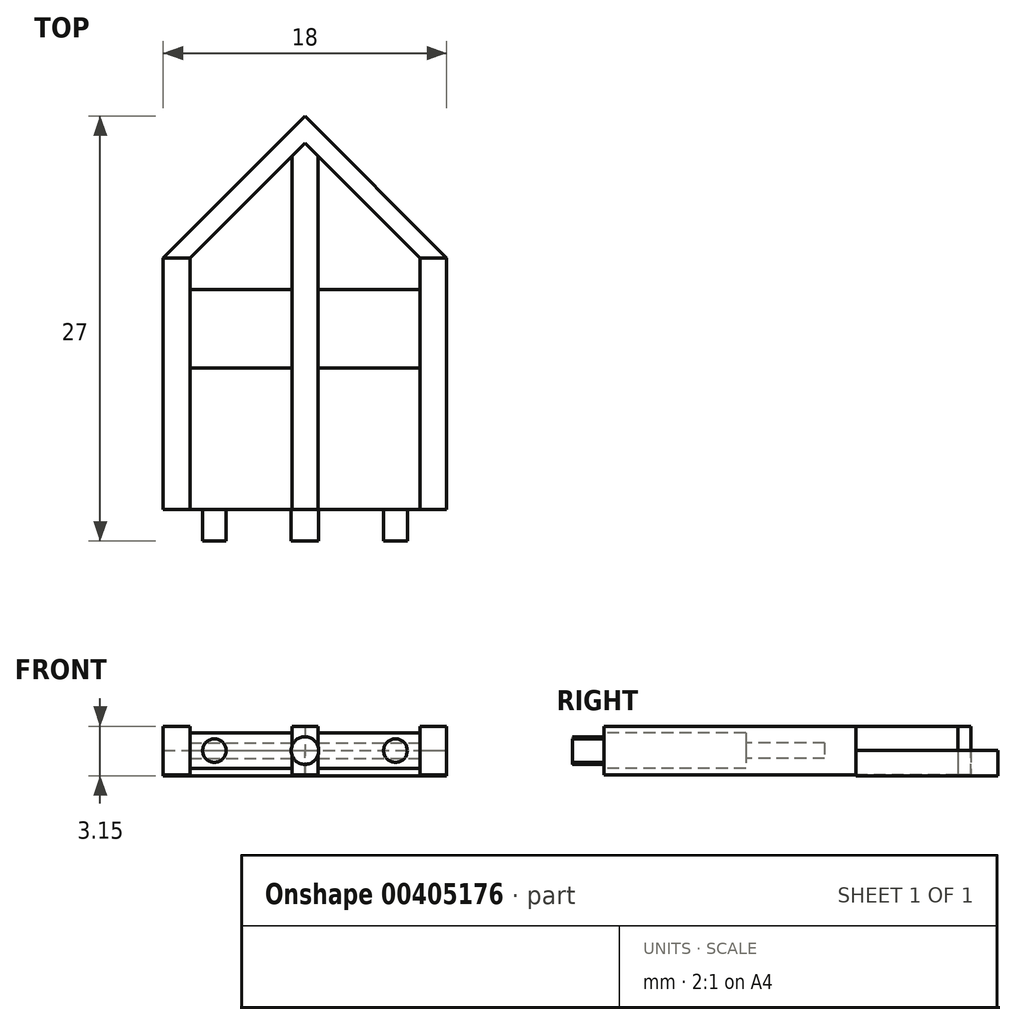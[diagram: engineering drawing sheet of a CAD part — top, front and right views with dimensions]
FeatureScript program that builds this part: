
annotation { "Feature Type Name" : "Feature", "Feature Type Description" : "" }
export const myFeature = defineFeature(function(context is Context, id is Id, definition is map)
    precondition{}
    {
        {
            var Q0;
            Q0=qCreatedBy(makeId("Top.planeOp"),FACE);
            var sketch = newSketch(context, id + "F0", { "sketchPlane" : qUnion([Q0])});
            skLineSegment(sketch, "E0", {"start": v(0, 0) * mm, "end": v(18, 0) * mm});
            skLineSegment(sketch, "E1", {"start": v(18, 0) * mm, "end": v(18, 16) * mm});
            skLineSegment(sketch, "E2", {"start": v(0, 16) * mm, "end": v(0, 0) * mm});
            skLineSegment(sketch, "E3", {"start": v(0, 16) * mm, "end": v(9, 25) * mm});
            skLineSegment(sketch, "E4", {"start": v(9, 25) * mm, "end": v(18, 16) * mm});
            skLineSegment(sketch, "E5", {"start": v(0, 9) * mm, "end": v(18, 9) * mm});
            skLineSegment(sketch, "E6", {"start": v(9, 25) * mm, "end": v(9, 0) * mm});
            skLineSegment(sketch, "E7", {"start": v(8.13, 0) * mm, "end": v(8.13, -2) * mm});
            skLineSegment(sketch, "E8", {"start": v(8.13, -2) * mm, "end": v(9.88, -2) * mm});
            skLineSegment(sketch, "E9", {"start": v(9.88, -2) * mm, "end": v(9.88, 0) * mm});
            skLineSegment(sketch, "E10", {"start": v(2.5, 0) * mm, "end": v(2.5, -2) * mm});
            skLineSegment(sketch, "E11", {"start": v(2.5, -2) * mm, "end": v(4, -2) * mm});
            skLineSegment(sketch, "E12", {"start": v(4, -2) * mm, "end": v(4, 0) * mm});
            skLineSegment(sketch, "E13", {"start": v(14, 0) * mm, "end": v(14, -2) * mm});
            skLineSegment(sketch, "E14", {"start": v(14, -2) * mm, "end": v(15.5, -2) * mm});
            skLineSegment(sketch, "E15", {"start": v(15.5, -2) * mm, "end": v(15.5, 0) * mm});
            skLineSegment(sketch, "E16", {"start": v(8.18, 22.47) * mm, "end": v(8.18, 0) * mm});
            skLineSegment(sketch, "E17", {"start": v(9.82, 22.47) * mm, "end": v(9.83, 0) * mm});
            skLineSegment(sketch, "E18", {"start": v(1.7, 16) * mm, "end": v(9, 23.3) * mm});
            skLineSegment(sketch, "E19", {"start": v(9, 23.3) * mm, "end": v(16.3, 16) * mm});
            skLineSegment(sketch, "E20", {"start": v(1.7, 16) * mm, "end": v(1.7, 0) * mm});
            skLineSegment(sketch, "E21", {"start": v(16.3, 16) * mm, "end": v(16.3, 0) * mm});
            skLineSegment(sketch, "E22", {"start": v(0, 14) * mm, "end": v(18, 14) * mm});
            skLineSegment(sketch, "E23", {"start": v(0, 16) * mm, "end": v(1.7, 16) * mm});
            skLineSegment(sketch, "E24", {"start": v(16.3, 16) * mm, "end": v(18, 16) * mm});
            skSolve(sketch);
        }
        {
            var Q0;
            {var subQ0=sQuery(id+"F0.wireOp",EDGE,"E2");var subQ1=sQuery(id+"F0.wireOp",EDGE,"E0");var subQ2=makeQuery(id+"F0.imprint","INTERSECT",VERTEX,{"derivedFrom":[subQ1,subQ0]});Q0=makeQuery(id+"F0.imprint","IMPRINT",FACE,{"disambiguationData":[TD([[makeQuery(id+"F0.imprint","IMPRINT",EDGE,{"disambiguationData":[TD([[subQ2,-1.0]])],"derivedFrom":subQ1}),1.0]])]});}
            var Q1;
            {var subQ0=sQuery(id+"F0.wireOp",EDGE,"E23");Q1=makeQuery(id+"F0.imprint","IMPRINT",FACE,{"disambiguationData":[TD([[makeQuery(id+"F0.imprint","IMPRINT",EDGE,{"derivedFrom":subQ0}),-1.0]])]});}
            var Q2;
            {var subQ0=sQuery(id+"F0.wireOp",EDGE,"E5");var subQ1=sQuery(id+"F0.wireOp",EDGE,"E2");var subQ2=makeQuery(id+"F0.imprint","INTERSECT",VERTEX,{"derivedFrom":[subQ1,subQ0]});Q2=makeQuery(id+"F0.imprint","IMPRINT",FACE,{"disambiguationData":[TD([[makeQuery(id+"F0.imprint","IMPRINT",EDGE,{"disambiguationData":[TD([[subQ2,1.0]])],"derivedFrom":subQ1}),1.0]])]});}
            var Q3;
            {var subQ0=sQuery(id+"F0.wireOp",EDGE,"E1");var subQ1=sQuery(id+"F0.wireOp",EDGE,"E0");var subQ2=makeQuery(id+"F0.imprint","INTERSECT",VERTEX,{"derivedFrom":[subQ1,subQ0]});Q3=makeQuery(id+"F0.imprint","IMPRINT",FACE,{"disambiguationData":[TD([[makeQuery(id+"F0.imprint","IMPRINT",EDGE,{"disambiguationData":[TD([[subQ2,1.0]])],"derivedFrom":subQ1}),1.0]])]});}
            var Q4;
            {var subQ0=sQuery(id+"F0.wireOp",EDGE,"E24");Q4=makeQuery(id+"F0.imprint","IMPRINT",FACE,{"disambiguationData":[TD([[makeQuery(id+"F0.imprint","IMPRINT",EDGE,{"derivedFrom":subQ0}),-1.0]])]});}
            var Q5;
            {var subQ0=sQuery(id+"F0.wireOp",EDGE,"E5");var subQ1=sQuery(id+"F0.wireOp",EDGE,"E1");var subQ2=makeQuery(id+"F0.imprint","INTERSECT",VERTEX,{"derivedFrom":[subQ1,subQ0]});Q5=makeQuery(id+"F0.imprint","IMPRINT",FACE,{"disambiguationData":[TD([[makeQuery(id+"F0.imprint","IMPRINT",EDGE,{"disambiguationData":[TD([[subQ2,-1.0]])],"derivedFrom":subQ1}),1.0]])]});}
            var Q6;
            {var subQ0=sQuery(id+"F0.wireOp",EDGE,"E6");var subQ1=sQuery(id+"F0.wireOp",EDGE,"E0");var subQ2=makeQuery(id+"F0.imprint","INTERSECT",VERTEX,{"derivedFrom":[subQ1,subQ0]});Q6=makeQuery(id+"F0.imprint","IMPRINT",FACE,{"disambiguationData":[TD([[makeQuery(id+"F0.imprint","IMPRINT",EDGE,{"disambiguationData":[TD([[subQ2,1.0]])],"derivedFrom":subQ1}),1.0]])]});}
            var Q7;
            {var subQ0=sQuery(id+"F0.wireOp",EDGE,"E6");var subQ1=sQuery(id+"F0.wireOp",EDGE,"E0");var subQ2=makeQuery(id+"F0.imprint","INTERSECT",VERTEX,{"derivedFrom":[subQ1,subQ0]});Q7=makeQuery(id+"F0.imprint","IMPRINT",FACE,{"disambiguationData":[TD([[makeQuery(id+"F0.imprint","IMPRINT",EDGE,{"disambiguationData":[TD([[subQ2,-1.0]])],"derivedFrom":subQ1}),1.0]])]});}
            var Q8;
            {var subQ0=sQuery(id+"F0.wireOp",EDGE,"E6");var subQ1=sQuery(id+"F0.wireOp",EDGE,"E5");var subQ2=makeQuery(id+"F0.imprint","INTERSECT",VERTEX,{"derivedFrom":[subQ1,subQ0]});Q8=makeQuery(id+"F0.imprint","IMPRINT",FACE,{"disambiguationData":[TD([[makeQuery(id+"F0.imprint","IMPRINT",EDGE,{"disambiguationData":[TD([[subQ2,-1.0]])],"derivedFrom":subQ1}),1.0]])]});}
            var Q9;
            {var subQ0=sQuery(id+"F0.wireOp",EDGE,"E16");var subQ1=sQuery(id+"F0.wireOp",EDGE,"E5");var subQ2=makeQuery(id+"F0.imprint","INTERSECT",VERTEX,{"derivedFrom":[subQ1,subQ0]});Q9=makeQuery(id+"F0.imprint","IMPRINT",FACE,{"disambiguationData":[TD([[makeQuery(id+"F0.imprint","IMPRINT",EDGE,{"disambiguationData":[TD([[subQ2,-1.0]])],"derivedFrom":subQ1}),1.0]])]});}
            var Q10;
            {var subQ0=sQuery(id+"F0.wireOp",EDGE,"E18");var subQ5=sQuery(id+"F0.wireOp",EDGE,"E16");var subQ7=makeQuery(id+"F0.imprint","INTERSECT",VERTEX,{"derivedFrom":[subQ5,subQ0]});Q10=makeQuery(id+"F0.imprint","IMPRINT",FACE,{"disambiguationData":[TD([[makeQuery(id+"F0.imprint","IMPRINT",EDGE,{"disambiguationData":[TD([[subQ7,-1.0]])],"derivedFrom":subQ5}),1.0]])]});}
            var Q11;
            {var subQ0=sQuery(id+"F0.wireOp",EDGE,"E19");var subQ5=sQuery(id+"F0.wireOp",EDGE,"E17");var subQ6=makeQuery(id+"F0.imprint","INTERSECT",VERTEX,{"derivedFrom":[subQ5,subQ0]});Q11=makeQuery(id+"F0.imprint","IMPRINT",FACE,{"disambiguationData":[TD([[makeQuery(id+"F0.imprint","IMPRINT",EDGE,{"disambiguationData":[TD([[subQ6,-1.0]])],"derivedFrom":subQ5}),-1.0]])]});}
            extrude(context, id + "F1", {"entities" : qUnion([Q0, Q1, Q2, Q3, Q4, Q5, Q6, Q7, Q8, Q9, Q10, Q11]), "endBound" : BoundingType.SYMMETRIC, "depth" : 3.1 * mm});
        }
        {
            var Q0;
            {var subQ0=sQuery(id+"F0.wireOp",EDGE,"E0");var subQ5=makeQuery(id+"F0.imprint","INTERSECT",VERTEX,{"derivedFrom":[subQ0,sQuery(id+"F0.wireOp",EDGE,"E10")]});Q0=makeQuery(id+"F0.imprint","IMPRINT",FACE,{"disambiguationData":[TD([[makeQuery(id+"F0.imprint","IMPRINT",EDGE,{"disambiguationData":[TD([[subQ5,1.0]])],"derivedFrom":subQ0}),1.0]])]});}
            var Q1;
            {var subQ0=sQuery(id+"F0.wireOp",EDGE,"E0");var subQ7=makeQuery(id+"F0.imprint","INTERSECT",VERTEX,{"derivedFrom":[subQ0,sQuery(id+"F0.wireOp",EDGE,"E9")]});Q1=makeQuery(id+"F0.imprint","IMPRINT",FACE,{"disambiguationData":[TD([[makeQuery(id+"F0.imprint","IMPRINT",EDGE,{"disambiguationData":[TD([[subQ7,1.0]])],"derivedFrom":subQ0}),1.0]])]});}
            extrude(context, id + "F2", {"entities" : qUnion([Q0, Q1]), "endBound" : BoundingType.SYMMETRIC, "depth" : 2.25 * mm});
        }
        {
            var Q0;
            {var subQ5=sQuery(id+"F0.wireOp",EDGE,"E3");Q0=makeQuery(id+"F0.imprint","IMPRINT",FACE,{"disambiguationData":[TD([[makeQuery(id+"F0.imprint","IMPRINT",EDGE,{"derivedFrom":subQ5}),-1.0]])]});}
            var Q1;
            {var subQ4=sQuery(id+"F0.wireOp",EDGE,"E4");Q1=makeQuery(id+"F0.imprint","IMPRINT",FACE,{"disambiguationData":[TD([[makeQuery(id+"F0.imprint","IMPRINT",EDGE,{"derivedFrom":subQ4}),-1.0]])]});}
            extrude(context, id + "F3", {"entities" : qUnion([Q0, Q1]), "oppositeDirection" : true, "depth" : 1.6 * mm});
        }
        {
            var Q0;
            {var subQ0=sQuery(id+"F0.wireOp",EDGE,"E20");var subQ1=sQuery(id+"F0.wireOp",EDGE,"E5");var subQ2=makeQuery(id+"F0.imprint","INTERSECT",VERTEX,{"derivedFrom":[subQ1,subQ0]});Q0=makeQuery(id+"F0.imprint","IMPRINT",FACE,{"disambiguationData":[TD([[makeQuery(id+"F0.imprint","IMPRINT",EDGE,{"disambiguationData":[TD([[subQ2,-1.0]])],"derivedFrom":subQ1}),1.0]])]});}
            var Q1;
            {var subQ0=sQuery(id+"F0.wireOp",EDGE,"E17");var subQ1=sQuery(id+"F0.wireOp",EDGE,"E5");var subQ2=makeQuery(id+"F0.imprint","INTERSECT",VERTEX,{"derivedFrom":[subQ1,subQ0]});Q1=makeQuery(id+"F0.imprint","IMPRINT",FACE,{"disambiguationData":[TD([[makeQuery(id+"F0.imprint","IMPRINT",EDGE,{"disambiguationData":[TD([[subQ2,-1.0]])],"derivedFrom":subQ1}),1.0]])]});}
            extrude(context, id + "F4", {"entities" : qUnion([Q0, Q1]), "endBound" : BoundingType.SYMMETRIC, "depth" : 1 * mm});
        }
        {
            var Q0;
            {var subQ0=sQuery(id+"F0.wireOp",EDGE,"E10");Q0=makeQuery(id+"F0.imprint","IMPRINT",FACE,{"disambiguationData":[TD([[makeQuery(id+"F0.imprint","IMPRINT",EDGE,{"derivedFrom":subQ0}),1.0]])]});}
            var Q1;
            {var subQ0=sQuery(id+"F0.wireOp",EDGE,"E13");Q1=makeQuery(id+"F0.imprint","IMPRINT",FACE,{"disambiguationData":[TD([[makeQuery(id+"F0.imprint","IMPRINT",EDGE,{"derivedFrom":subQ0}),1.0]])]});}
            extrude(context, id + "F5", {"entities" : qUnion([Q0, Q1]), "endBound" : BoundingType.SYMMETRIC, "depth" : 1.5 * mm});
        }
        {
            var Q0;
            {var subQ5=sQuery(id+"F0.wireOp",EDGE,"E7");Q0=makeQuery(id+"F0.imprint","IMPRINT",FACE,{"disambiguationData":[TD([[makeQuery(id+"F0.imprint","IMPRINT",EDGE,{"derivedFrom":subQ5}),1.0]])]});}
            extrude(context, id + "F6", {"entities" : qUnion([Q0]), "endBound" : BoundingType.SYMMETRIC, "depth" : 1.75 * mm});
        }
        {
            var Q0;
            Q0=makeQuery(id+"F6.opExtrude","CAP_EDGE",EDGE,{"disambiguationData":[OSD([sQuery(id+"F0.wireOp",EDGE,"E9")])],"isStart":true});
            var Q1;
            Q1=makeQuery(id+"F6.opExtrude","CAP_EDGE",EDGE,{"disambiguationData":[OSD([sQuery(id+"F0.wireOp",EDGE,"E7")])],"isStart":true});
            var Q2;
            Q2=makeQuery(id+"F6.opExtrude","CAP_EDGE",EDGE,{"disambiguationData":[OSD([sQuery(id+"F0.wireOp",EDGE,"E9")])],"isStart":false});
            var Q3;
            Q3=makeQuery(id+"F6.opExtrude","CAP_EDGE",EDGE,{"disambiguationData":[OSD([sQuery(id+"F0.wireOp",EDGE,"E7")])],"isStart":false});
            fillet(context, id + "F7", {"entities" : qUnion([Q0, Q1, Q2, Q3]), "radius" : 0.88 * mm, "tangentPropagation" : true, "allowEdgeOverflow" : false});
        }
        {
            var Q0;
            Q0=makeQuery(id+"F5.opExtrude","CAP_EDGE",EDGE,{"disambiguationData":[OSD([sQuery(id+"F0.wireOp",EDGE,"E13")])],"isStart":false});
            var Q1;
            Q1=makeQuery(id+"F5.opExtrude","CAP_EDGE",EDGE,{"disambiguationData":[OSD([sQuery(id+"F0.wireOp",EDGE,"E15")])],"isStart":false});
            var Q2;
            Q2=makeQuery(id+"F5.opExtrude","CAP_EDGE",EDGE,{"disambiguationData":[OSD([sQuery(id+"F0.wireOp",EDGE,"E15")])],"isStart":true});
            var Q3;
            Q3=makeQuery(id+"F5.opExtrude","CAP_EDGE",EDGE,{"disambiguationData":[OSD([sQuery(id+"F0.wireOp",EDGE,"E13")])],"isStart":true});
            var Q4;
            Q4=makeQuery(id+"F5.opExtrude","CAP_EDGE",EDGE,{"disambiguationData":[OSD([sQuery(id+"F0.wireOp",EDGE,"E10")])],"isStart":false});
            var Q5;
            Q5=makeQuery(id+"F5.opExtrude","CAP_EDGE",EDGE,{"disambiguationData":[OSD([sQuery(id+"F0.wireOp",EDGE,"E12")])],"isStart":false});
            var Q6;
            Q6=makeQuery(id+"F5.opExtrude","CAP_EDGE",EDGE,{"disambiguationData":[OSD([sQuery(id+"F0.wireOp",EDGE,"E10")])],"isStart":true});
            var Q7;
            Q7=makeQuery(id+"F5.opExtrude","CAP_EDGE",EDGE,{"disambiguationData":[OSD([sQuery(id+"F0.wireOp",EDGE,"E12")])],"isStart":true});
            fillet(context, id + "F8", {"entities" : qUnion([Q0, Q1, Q2, Q3, Q4, Q5, Q6, Q7]), "radius" : 0.75 * mm, "tangentPropagation" : true, "allowEdgeOverflow" : false});
        }
    });
